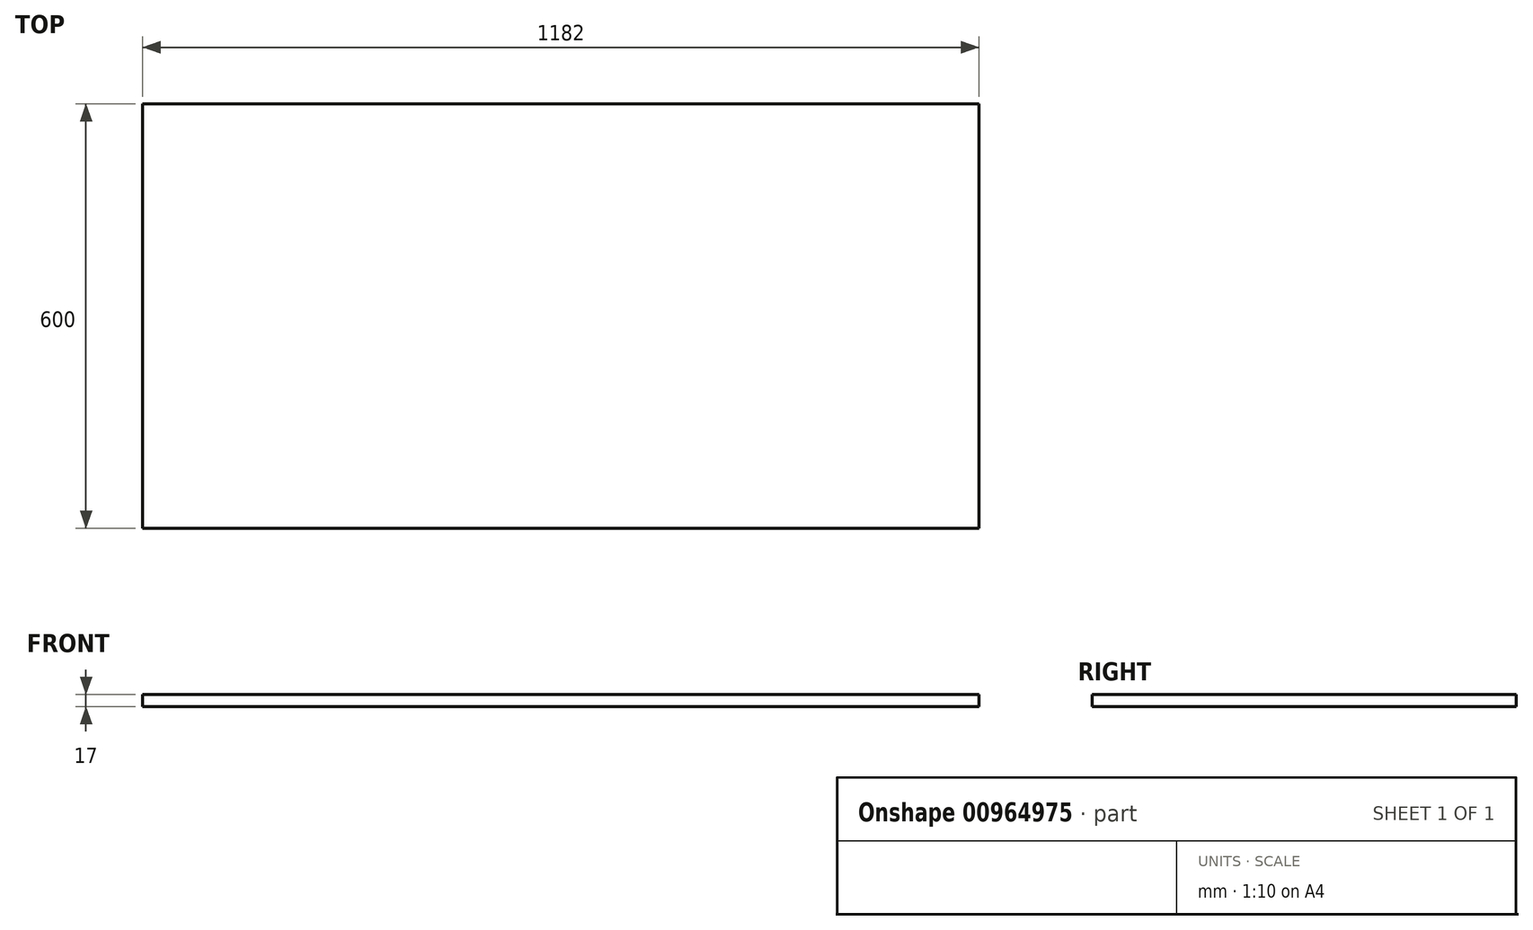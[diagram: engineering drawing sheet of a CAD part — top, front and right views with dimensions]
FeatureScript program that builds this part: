
annotation { "Feature Type Name" : "Feature", "Feature Type Description" : "" }
export const myFeature = defineFeature(function(context is Context, id is Id, definition is map)
    precondition{}
    {
        {
            var Q0;
            Q0=qCreatedBy(makeId("Top.planeOp"),FACE);
            var sketch = newSketch(context, id + "F0", { "sketchPlane" : qUnion([Q0])});
            skLineSegment(sketch, "E0.bottom", {"start": v(-498.01, 300) * mm, "end": v(683.99, 300) * mm});
            skLineSegment(sketch, "E0.top", {"start": v(-498.01, -300) * mm, "end": v(683.99, -300) * mm});
            skLineSegment(sketch, "E0.left", {"start": v(-498.01, 300) * mm, "end": v(-498.01, -300) * mm});
            skLineSegment(sketch, "E0.right", {"start": v(683.99, 300) * mm, "end": v(683.99, -300) * mm});
            skPoint(sketch, "E0.middle", {"position": v(92.99, 0) * mm});
            skSolve(sketch);
        }
        {
            var Q0;
            Q0=makeQuery(id+"F0.imprint","IMPRINT",FACE,{"disambiguationData":[TD([[makeQuery(id+"F0.imprint","IMPRINT",EDGE,{"derivedFrom":sQuery(id+"F0.wireOp",EDGE,"E0.bottom")}),-1.0]])]});
            extrude(context, id + "F1", {"entities" : qUnion([Q0]), "depth" : 17 * mm, "offsetDistance" : 25 * mm});
        }
    });
